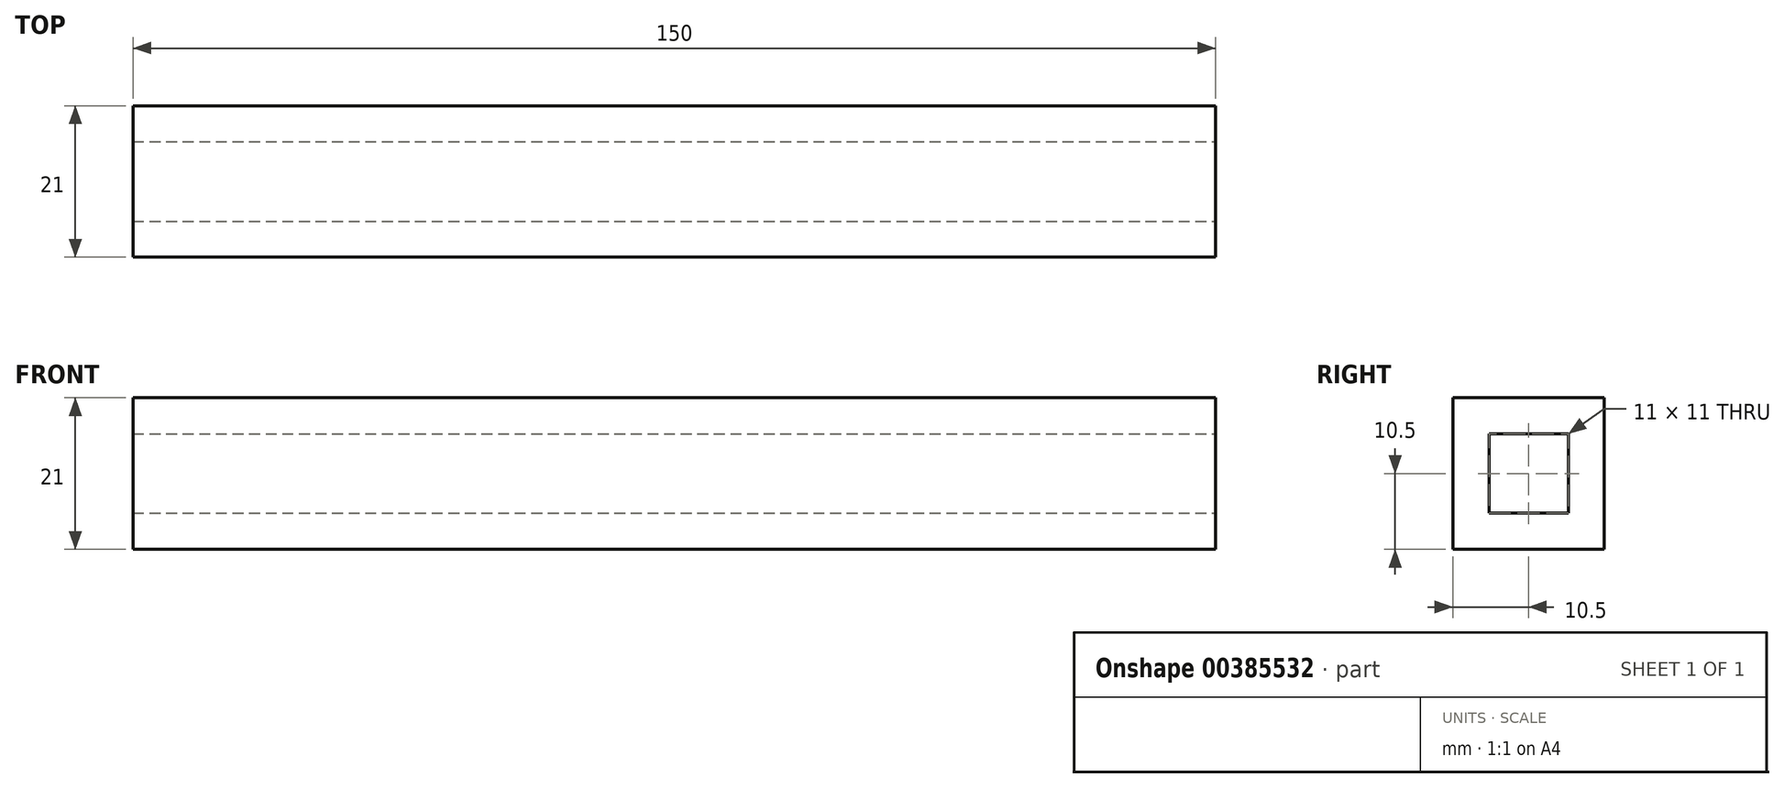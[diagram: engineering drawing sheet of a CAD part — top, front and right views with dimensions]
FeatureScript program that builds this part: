
annotation { "Feature Type Name" : "Feature", "Feature Type Description" : "" }
export const myFeature = defineFeature(function(context is Context, id is Id, definition is map)
    precondition{}
    {
        {
            var Q0;
            Q0=qCreatedBy(makeId("Front.planeOp"),FACE);
            var sketch = newSketch(context, id + "F0", { "sketchPlane" : qUnion([Q0])});
            skLineSegment(sketch, "E0.bottom", {"start": v(0, 0) * mm, "end": v(-150, 0) * mm});
            skLineSegment(sketch, "E0.top", {"start": v(0, 21) * mm, "end": v(-150, 21) * mm});
            skLineSegment(sketch, "E0.left", {"start": v(0, 0) * mm, "end": v(0, 21) * mm});
            skLineSegment(sketch, "E0.right", {"start": v(-150, 0) * mm, "end": v(-150, 21) * mm});
            skSolve(sketch);
        }
        {
            var Q0;
            Q0=qSketchRegion(id+"F0",true);
            extrude(context, id + "F1", {"entities" : qUnion([Q0]), "depth" : 21 * mm});
        }
        {
            var Q0;
            Q0=qCreatedBy(makeId("Right.planeOp"),FACE);
            var sketch = newSketch(context, id + "F2", { "sketchPlane" : qUnion([Q0])});
            skLineSegment(sketch, "E1.0", {"start": v(-5, 5) * mm, "end": v(-5, 16) * mm});
            skLineSegment(sketch, "E1.1", {"start": v(-16, 5) * mm, "end": v(-5, 5) * mm});
            skLineSegment(sketch, "E1.2", {"start": v(-16, 16) * mm, "end": v(-16, 5) * mm});
            skLineSegment(sketch, "E1.3", {"start": v(-5, 16) * mm, "end": v(-16, 16) * mm});
            skSolve(sketch);
        }
        {
            var Q0;
            Q0=makeQuery(id+"F2.imprint","IMPRINT",FACE,{"disambiguationData":[TD([[makeQuery(id+"F2.imprint","IMPRINT",EDGE,{"derivedFrom":sQuery(id+"F2.wireOp",EDGE,"E1.0")}),1.0]])]});
            extrude(context, id + "F3", {"entities" : qUnion([Q0]), "operationType" : NewBodyOperationType.REMOVE, "oppositeDirection" : true, "depth" : 200 * mm});
        }
    });
